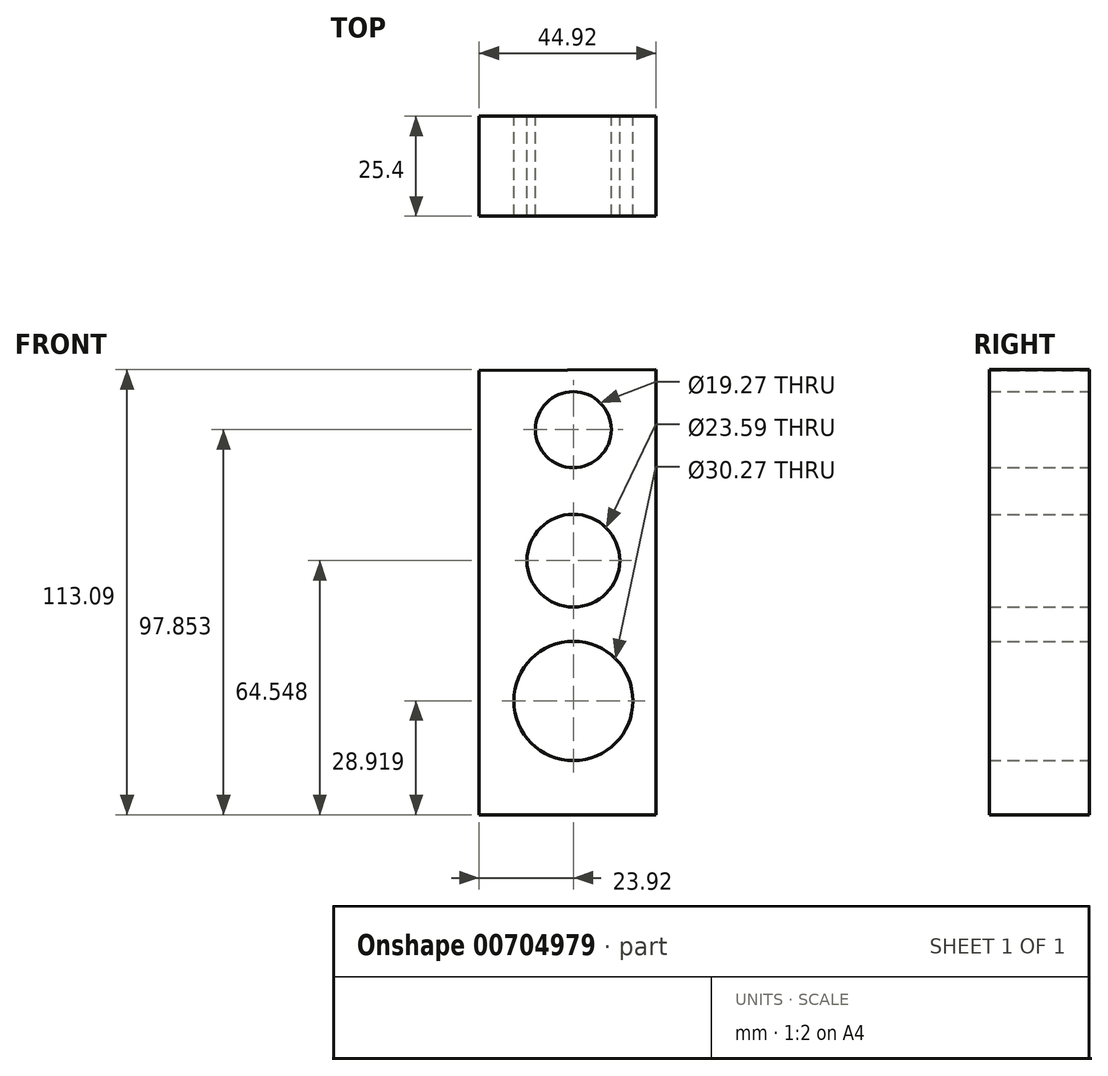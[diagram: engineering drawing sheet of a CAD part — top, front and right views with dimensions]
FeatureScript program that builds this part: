
annotation { "Feature Type Name" : "Feature", "Feature Type Description" : "" }
export const myFeature = defineFeature(function(context is Context, id is Id, definition is map)
    precondition{}
    {
        {
            var Q0;
            Q0=qCreatedBy(makeId("Front.planeOp"),FACE);
            var sketch = newSketch(context, id + "F0", { "sketchPlane" : qUnion([Q0])});
            skLineSegment(sketch, "E0", {"start": v(-23.92, 56.04) * mm, "end": v(-23.92, -56.79) * mm});
            skLineSegment(sketch, "E1", {"start": v(-23.92, -56.79) * mm, "end": v(21, -56.79) * mm});
            skLineSegment(sketch, "E2", {"start": v(21, -56.79) * mm, "end": v(21, 56.3) * mm});
            skLineSegment(sketch, "E3", {"start": v(21, 56.3) * mm, "end": v(-23.92, 56.04) * mm});
            skCircle(sketch, "E4", {"center": v(0, 41.06) * mm, "radius": 9.64 * mm});
            skCircle(sketch, "E5", {"center": v(0, 7.76) * mm, "radius": 11.8 * mm});
            skCircle(sketch, "E6", {"center": v(0, -27.87) * mm, "radius": 15.13 * mm});
            skSolve(sketch);
        }
        {
            var Q0;
            Q0=makeQuery(id+"F0.imprint","IMPRINT",FACE,{"disambiguationData":[TD([[makeQuery(id+"F0.imprint","IMPRINT",EDGE,{"derivedFrom":sQuery(id+"F0.wireOp",EDGE,"E0")}),1.0]])]});
            extrude(context, id + "F1", {"entities" : qUnion([Q0]), "depth" : 25.4 * mm, "offsetDistance" : 25.4 * mm});
        }
    });
